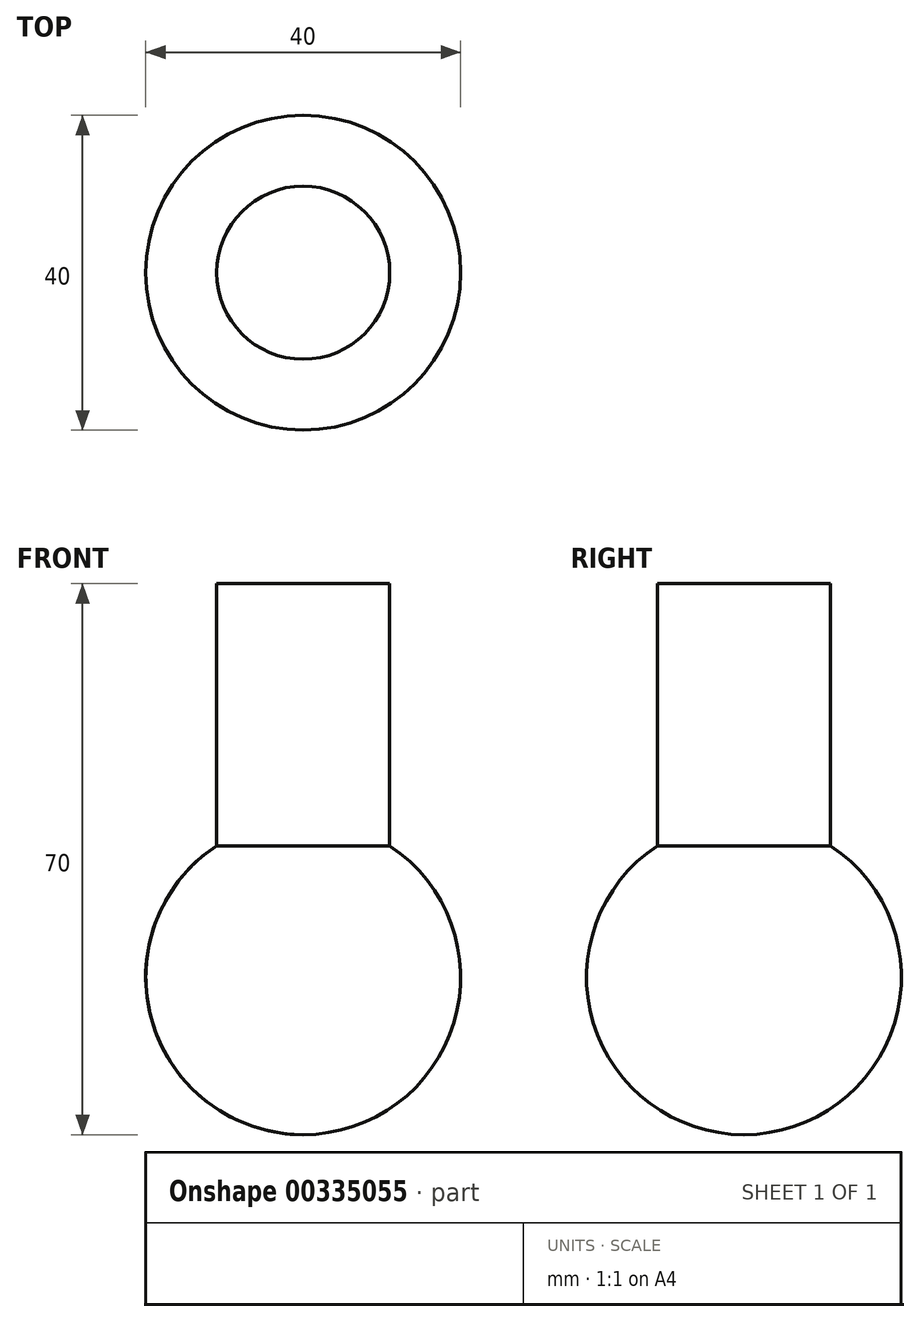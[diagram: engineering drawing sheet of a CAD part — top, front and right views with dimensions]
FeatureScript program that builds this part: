
annotation { "Feature Type Name" : "Feature", "Feature Type Description" : "" }
export const myFeature = defineFeature(function(context is Context, id is Id, definition is map)
    precondition{}
    {
        {
            var Q0;
            Q0=qCreatedBy(makeId("Front.planeOp"),FACE);
            var sketch = newSketch(context, id + "F0", { "sketchPlane" : qUnion([Q0])});
            skLineSegment(sketch, "E0", {"start": v(0, 0) * mm, "end": v(0, 70) * mm});
            skLineSegment(sketch, "E1", {"start": v(0, 70) * mm, "end": v(11, 70) * mm});
            skLineSegment(sketch, "E2", {"start": v(11, 70) * mm, "end": v(11, 36.7) * mm});
            skArc(sketch, "E3", {"start": v(0, 0) * mm, "mid": v(19.16, 14.26) * mm, "end": v(11, 36.7) * mm});
            skLineSegment(sketch, "E4", {"start": v(0, 70) * mm, "end": v(0, 94.29) * mm, "construction": true});
            skLineSegment(sketch, "E5", {"start": v(0, 0) * mm, "end": v(36.6, 0) * mm, "construction": true});
            skSolve(sketch);
        }
        {
            var Q0;
            Q0=makeQuery(id+"F0.imprint","IMPRINT",FACE,{"disambiguationData":[TD([[makeQuery(id+"F0.imprint","IMPRINT",EDGE,{"derivedFrom":sQuery(id+"F0.wireOp",EDGE,"E0")}),-1.0]])]});
            var Q1;
            Q1=sQuery(id+"F0.wireOp",EDGE,"E4");
            revolve(context, id + "F1", {"entities" : qUnion([Q0]), "axis" : qUnion([Q1]), "revolveType" : RevolveType.FULL});
        }
    });
